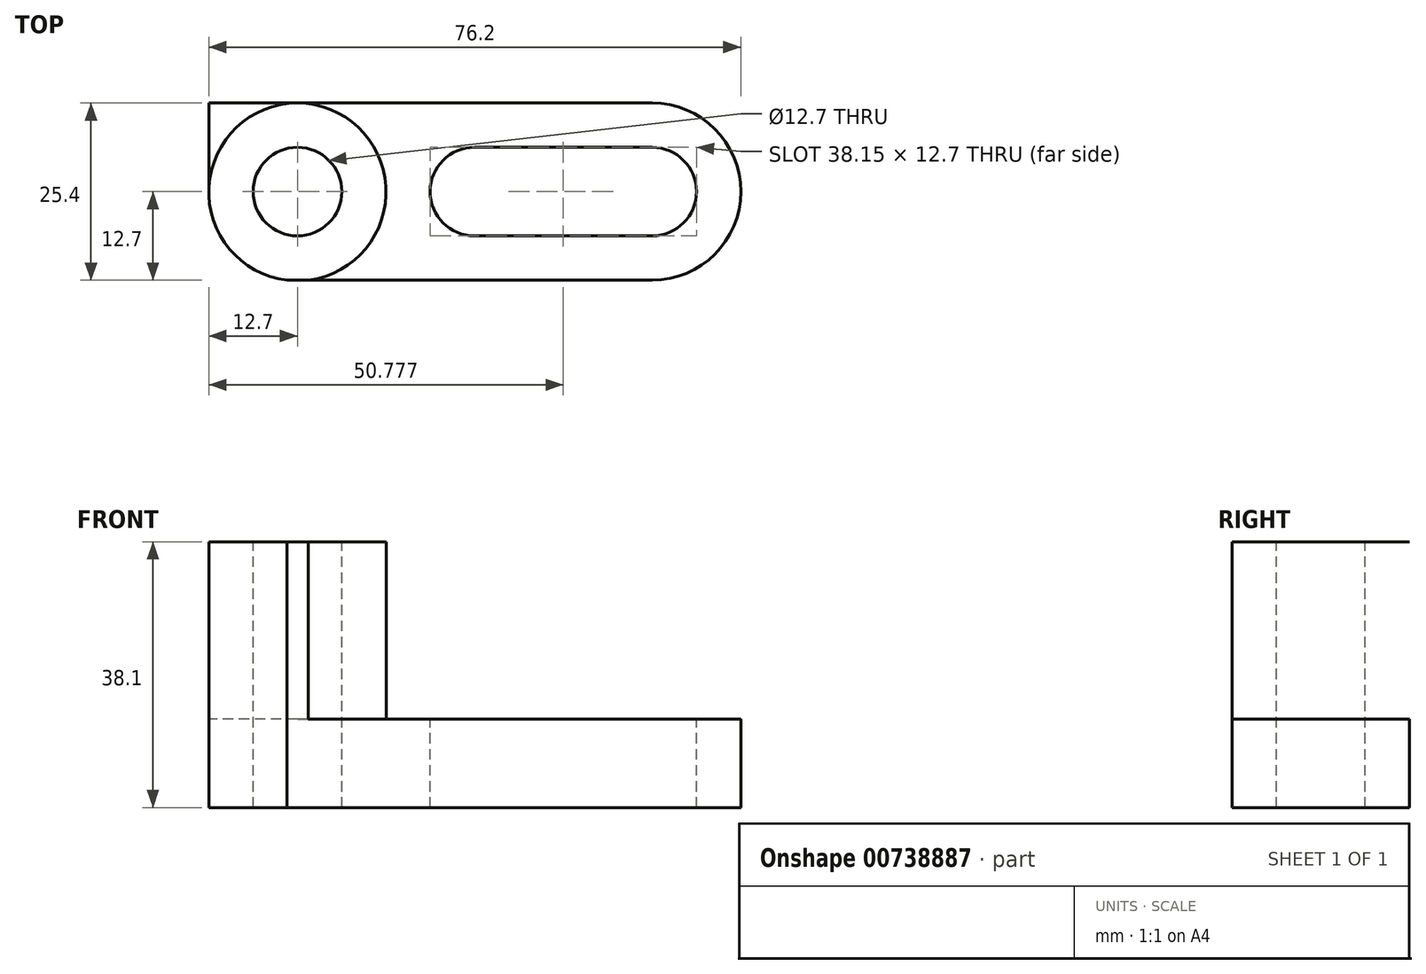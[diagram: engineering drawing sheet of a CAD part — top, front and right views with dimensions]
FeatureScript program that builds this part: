
annotation { "Feature Type Name" : "Feature", "Feature Type Description" : "" }
export const myFeature = defineFeature(function(context is Context, id is Id, definition is map)
    precondition{}
    {
        {
            var Q0;
            Q0=qCreatedBy(makeId("Front.planeOp"),FACE);
            var sketch = newSketch(context, id + "F0", { "sketchPlane" : qUnion([Q0])});
            skLineSegment(sketch, "E0", {"start": v(0, 38.1) * mm, "end": v(0, 0) * mm});
            skLineSegment(sketch, "E1", {"start": v(0, 0) * mm, "end": v(76.2, 0) * mm});
            skLineSegment(sketch, "E2", {"start": v(76.2, 0) * mm, "end": v(76.2, 38.1) * mm});
            skLineSegment(sketch, "E3", {"start": v(76.2, 38.1) * mm, "end": v(0, 38.1) * mm});
            skSolve(sketch);
        }
        {
            var Q0;
            Q0=makeQuery(id+"F0.imprint","IMPRINT",FACE,{"disambiguationData":[TD([[makeQuery(id+"F0.imprint","IMPRINT",EDGE,{"derivedFrom":sQuery(id+"F0.wireOp",EDGE,"E0")}),1.0]])]});
            extrude(context, id + "F1", {"entities" : qUnion([Q0]), "depth" : 25.4 * mm, "offsetDistance" : 25.4 * mm});
        }
        {
            var Q0;
            Q0=makeQuery(id+"F1.opExtrude","CAP_FACE",FACE,{"disambiguationData":[OSD([sQuery(id+"F0.wireOp",EDGE,"E0"),sQuery(id+"F0.wireOp",EDGE,"E1"),sQuery(id+"F0.wireOp",EDGE,"E2"),sQuery(id+"F0.wireOp",EDGE,"E3")])],"isStart":false});
            var sketch = newSketch(context, id + "F2", { "sketchPlane" : qUnion([Q0])});
            skLineSegment(sketch, "E4", {"start": v(25.4, 38.1) * mm, "end": v(25.4, 12.7) * mm});
            skLineSegment(sketch, "E5", {"start": v(25.4, 12.7) * mm, "end": v(76.2, 12.7) * mm});
            skSolve(sketch);
        }
        {
            var Q0;
            Q0 = qSketchRegion(id + "F2", true);
            var Q1;
            {var subQ0=sQuery(id+"F2.wireOp",EDGE,"E4");Q1=makeQuery(id+"F2.imprint","IMPRINT",FACE,{"disambiguationData":[TD([[makeQuery(id+"F2.imprint","IMPRINT",EDGE,{"derivedFrom":subQ0}),1.0]])]});}
            extrude(context, id + "F3", {"entities" : qUnion([Q0, Q1]), "operationType" : NewBodyOperationType.REMOVE, "oppositeDirection" : true, "depth" : 25.4 * mm, "offsetDistance" : 25.4 * mm});
        }
        {
            var Q0;
            Q0=makeQuery(id+"F1.opExtrude","SWEPT_FACE",FACE,{"disambiguationData":[OSD([sQuery(id+"F0.wireOp",EDGE,"E3")])]});
            var sketch = newSketch(context, id + "F4", { "sketchPlane" : qUnion([Q0])});
            skCircle(sketch, "E6", {"center": v(12.7, -12.7) * mm, "radius": 6.35 * mm});
            skArc(sketch, "E7", {"start": v(12.7, 0) * mm, "mid": v(0.02, -13.54) * mm, "end": v(14.28, -25.4) * mm});
            skArc(sketch, "E8", {"start": v(14.28, -25.4) * mm, "mid": v(25.38, -11.96) * mm, "end": v(12.7, 0) * mm});
            skSolve(sketch);
        }
        {
            var Q0;
            {var subQ0=sQuery(id+"F4.wireOp",EDGE,"E7");var subQ1=makeQuery(id+"F1.opExtrude","CAP_EDGE",EDGE,{"disambiguationData":[OSD([sQuery(id+"F0.wireOp",EDGE,"E3")])],"isStart":false});var subQ3=makeQuery(id+"F4.imprint","INTERSECT",VERTEX,{"derivedFrom":[subQ1,subQ0]});Q0=makeQuery(id+"F4.imprint","IMPRINT",FACE,{"disambiguationData":[TD([[makeQuery(id+"F4.imprint","IMPRINT",EDGE,{"disambiguationData":[TD([[subQ3,-1.0]])],"derivedFrom":subQ0}),1.0]])]});}
            var Q1;
            Q1=makeQuery(id+"F4.imprint","IMPRINT",FACE,{"disambiguationData":[TD([[makeQuery(id+"F4.imprint","IMPRINT",EDGE,{"derivedFrom":sQuery(id+"F4.wireOp",EDGE,"E6")}),1.0]])]});
            var Q2;
            {var subQ0=sQuery(id+"F4.wireOp",EDGE,"E7");var subQ1=sQuery(id+"F0.wireOp",EDGE,"E3");var subQ2=makeQuery(id+"F1.opExtrude","CAP_EDGE",EDGE,{"disambiguationData":[OSD([subQ1])],"isStart":true});var subQ3=makeQuery(id+"F4.imprint","INTERSECT",VERTEX,{"derivedFrom":[subQ2,subQ0,sQuery(id+"F4.wireOp",EDGE,"E8")]});Q2=makeQuery(id+"F4.imprint","IMPRINT",FACE,{"disambiguationData":[TD([[makeQuery(id+"F4.imprint","IMPRINT",EDGE,{"disambiguationData":[TD([[subQ3,-1.0]])],"derivedFrom":subQ0}),-1.0]])]});}
            var Q3;
            {var subQ0=sQuery(id+"F4.wireOp",EDGE,"E8");var subQ1=sQuery(id+"F0.wireOp",EDGE,"E3");var subQ2=makeQuery(id+"F1.opExtrude","CAP_EDGE",EDGE,{"disambiguationData":[OSD([subQ1])],"isStart":true});var subQ3=makeQuery(id+"F4.imprint","INTERSECT",VERTEX,{"derivedFrom":[subQ2,sQuery(id+"F4.wireOp",EDGE,"E7"),subQ0]});Q3=makeQuery(id+"F4.imprint","IMPRINT",FACE,{"disambiguationData":[TD([[makeQuery(id+"F4.imprint","IMPRINT",EDGE,{"disambiguationData":[TD([[subQ3,1.0]])],"derivedFrom":subQ0}),-1.0]])]});}
            var Q4;
            {var subQ0=sQuery(id+"F4.wireOp",EDGE,"E8");var subQ1=sQuery(id+"F0.wireOp",EDGE,"E3");var subQ2=makeQuery(id+"F1.opExtrude","CAP_EDGE",EDGE,{"disambiguationData":[OSD([subQ1])],"isStart":false});var subQ3=makeQuery(id+"F4.imprint","INTERSECT",VERTEX,{"derivedFrom":[subQ2,sQuery(id+"F4.wireOp",EDGE,"E7"),subQ0]});Q4=makeQuery(id+"F4.imprint","IMPRINT",FACE,{"disambiguationData":[TD([[makeQuery(id+"F4.imprint","IMPRINT",EDGE,{"disambiguationData":[TD([[subQ3,-1.0]])],"derivedFrom":subQ0}),-1.0]])]});}
            var Q5;
            {var subQ0=sQuery(id+"F4.wireOp",EDGE,"E7");var subQ1=sQuery(id+"F0.wireOp",EDGE,"E3");var subQ4=makeQuery(id+"F1.opExtrude","CAP_EDGE",EDGE,{"disambiguationData":[OSD([subQ1])],"isStart":false});var subQ5=makeQuery(id+"F4.imprint","INTERSECT",VERTEX,{"derivedFrom":[subQ4,subQ0]});Q5=makeQuery(id+"F4.imprint","IMPRINT",FACE,{"disambiguationData":[TD([[makeQuery(id+"F4.imprint","IMPRINT",EDGE,{"disambiguationData":[TD([[subQ5,1.0]])],"derivedFrom":subQ0}),-1.0]])]});}
            extrude(context, id + "F5", {"entities" : qUnion([Q0, Q1, Q2, Q3, Q4, Q5]), "operationType" : NewBodyOperationType.REMOVE, "oppositeDirection" : true, "depth" : 25.4 * mm, "offsetDistance" : 25.4 * mm});
        }
        {
            var Q0;
            {var subQ0=sQuery(id+"F0.wireOp",EDGE,"E3");var subQ1=makeQuery(id+"F1.opExtrude","CAP_EDGE",EDGE,{"disambiguationData":[OSD([subQ0])],"isStart":true});var subQ2=sQuery(id+"F0.wireOp",EDGE,"E0");var subQ3=makeQuery(id+"F1.opExtrude","SWEPT_EDGE",EDGE,{"disambiguationData":[OSD([subQ2,subQ0])]});var subQ4=makeQuery(id+"F4.imprint","INTERSECT",VERTEX,{"derivedFrom":[subQ3,subQ1]});var subQ5=sQuery(id+"F4.wireOp",EDGE,"E7");var subQ6=makeQuery(id+"F4.imprint","INTERSECT",VERTEX,{"derivedFrom":[subQ1,subQ5,sQuery(id+"F4.wireOp",EDGE,"E8")]});Q0=makeQuery(id+"F5.boolean.opBoolean","COPY",FACE,{"derivedFrom":makeQuery(id+"F5.opExtrude","CAP_FACE",FACE,{"disambiguationData":[OSD([subQ2,subQ0,subQ5]),TDD([makeQuery(id+"F4.imprint","IMPRINT",EDGE,{"disambiguationData":[TD([[subQ6,-1.0]])],"derivedFrom":subQ5}),makeQuery(id+"F4.imprint","IMPRINT",EDGE,{"disambiguationData":[TD([[subQ4,1.0]])],"derivedFrom":subQ3}),makeQuery(id+"F4.imprint","IMPRINT",EDGE,{"disambiguationData":[TD([[subQ4,1.0]])],"derivedFrom":subQ1})])],"isStart":false})});}
            var sketch = newSketch(context, id + "F6", { "sketchPlane" : qUnion([Q0])});
            skSolve(sketch);
        }
        {
            var Q0;
            Q0 = qSketchRegion(id + "F6", true);
            var Q1;
            {var subQ0=sQuery(id+"F4.wireOp",EDGE,"E7");var subQ1=sQuery(id+"F0.wireOp",EDGE,"E3");var subQ2=makeQuery(id+"F1.opExtrude","CAP_EDGE",EDGE,{"disambiguationData":[OSD([subQ1])],"isStart":true});var subQ3=makeQuery(id+"F4.imprint","INTERSECT",VERTEX,{"derivedFrom":[subQ2,subQ0,sQuery(id+"F4.wireOp",EDGE,"E8")]});Q1=makeQuery(id+"F6.imprint","IMPRINT",FACE,{"disambiguationData":[TD([[makeQuery(id+"F6.imprint","IMPRINT",EDGE,{"derivedFrom":makeQuery(id+"F5.boolean.opBoolean","COPY",EDGE,{"derivedFrom":makeQuery(id+"F5.opExtrude","CAP_EDGE",EDGE,{"disambiguationData":[OSD([subQ0]),TDD([makeQuery(id+"F4.imprint","IMPRINT",EDGE,{"disambiguationData":[TD([[subQ3,-1.0]])],"derivedFrom":subQ0})])],"isStart":false})})}),-1.0]])]});}
            var Q2;
            {var subQ0=sQuery(id+"F0.wireOp",EDGE,"E3");var subQ1=makeQuery(id+"F1.opExtrude","CAP_EDGE",EDGE,{"disambiguationData":[OSD([subQ0])],"isStart":false});var subQ2=sQuery(id+"F0.wireOp",EDGE,"E0");var subQ3=makeQuery(id+"F1.opExtrude","SWEPT_EDGE",EDGE,{"disambiguationData":[OSD([subQ2,subQ0])]});var subQ4=makeQuery(id+"F4.imprint","INTERSECT",VERTEX,{"derivedFrom":[subQ3,subQ1]});var subQ5=sQuery(id+"F4.wireOp",EDGE,"E7");var subQ6=makeQuery(id+"F4.imprint","INTERSECT",VERTEX,{"derivedFrom":[subQ1,subQ5]});Q2=makeQuery(id+"F5.boolean.opBoolean","COPY",FACE,{"derivedFrom":makeQuery(id+"F5.opExtrude","CAP_FACE",FACE,{"disambiguationData":[OSD([subQ2,subQ0,subQ5]),TDD([makeQuery(id+"F4.imprint","IMPRINT",EDGE,{"disambiguationData":[TD([[subQ6,1.0]])],"derivedFrom":subQ5}),makeQuery(id+"F4.imprint","IMPRINT",EDGE,{"disambiguationData":[TD([[subQ4,-1.0]])],"derivedFrom":subQ3}),makeQuery(id+"F4.imprint","IMPRINT",EDGE,{"disambiguationData":[TD([[subQ6,-1.0]])],"derivedFrom":subQ1})])],"isStart":false})});}
            extrude(context, id + "F7", {"entities" : qUnion([Q0, Q1, Q2]), "operationType" : NewBodyOperationType.REMOVE, "oppositeDirection" : true, "depth" : 25.4 * mm, "offsetDistance" : 25.4 * mm});
        }
        {
            var Q0;
            Q0=makeQuery(id+"F5.boolean.opBoolean","COPY",FACE,{"derivedFrom":makeQuery(id+"F5.opExtrude","CAP_FACE",FACE,{"disambiguationData":[OSD([sQuery(id+"F4.wireOp",EDGE,"E6")])],"isStart":false})});
            extrude(context, id + "F8", {"entities" : qUnion([Q0]), "operationType" : NewBodyOperationType.REMOVE, "oppositeDirection" : true, "depth" : 25.4 * mm, "offsetDistance" : 25.4 * mm});
        }
        {
            var Q0;
            {var subQ0=sQuery(id+"F0.wireOp",EDGE,"E3");var subQ1=makeQuery(id+"F1.opExtrude","CAP_EDGE",EDGE,{"disambiguationData":[OSD([subQ0])],"isStart":true});var subQ2=sQuery(id+"F2.wireOp",EDGE,"E4");var subQ3=makeQuery(id+"F3.boolean.opBoolean","COPY",EDGE,{"derivedFrom":makeQuery(id+"F3.opExtrude","SWEPT_EDGE",EDGE,{"disambiguationData":[OSD([subQ0,subQ2])]})});var subQ4=makeQuery(id+"F4.imprint","INTERSECT",VERTEX,{"derivedFrom":[subQ3,subQ1]});var subQ5=sQuery(id+"F4.wireOp",EDGE,"E8");var subQ6=sQuery(id+"F4.wireOp",EDGE,"E7");var subQ7=makeQuery(id+"F4.imprint","INTERSECT",VERTEX,{"derivedFrom":[subQ1,subQ6,subQ5]});var subQ9=makeQuery(id+"F1.opExtrude","CAP_EDGE",EDGE,{"disambiguationData":[OSD([subQ0])],"isStart":false});var subQ10=makeQuery(id+"F4.imprint","INTERSECT",VERTEX,{"derivedFrom":[subQ3,subQ9]});var subQ11=makeQuery(id+"F4.imprint","INTERSECT",VERTEX,{"derivedFrom":[subQ9,subQ6,subQ5]});Q0=makeQuery(id+"F5.boolean.opBoolean","MERGE",FACE,{"derivedFrom":[makeQuery(id+"F3.boolean.opBoolean","COPY",FACE,{"derivedFrom":makeQuery(id+"F3.opExtrude","SWEPT_FACE",FACE,{"disambiguationData":[OSD([sQuery(id+"F2.wireOp",EDGE,"E5")])]})}),makeQuery(id+"F5.opExtrude","CAP_FACE",FACE,{"disambiguationData":[OSD([subQ0,subQ2,subQ5]),TDD([makeQuery(id+"F4.imprint","IMPRINT",EDGE,{"disambiguationData":[TD([[subQ11,-1.0]])],"derivedFrom":subQ5}),makeQuery(id+"F4.imprint","IMPRINT",EDGE,{"disambiguationData":[TD([[subQ10,1.0]])],"derivedFrom":subQ3}),makeQuery(id+"F4.imprint","IMPRINT",EDGE,{"disambiguationData":[TD([[subQ10,-1.0]])],"derivedFrom":subQ9})])],"isStart":false}),makeQuery(id+"F5.opExtrude","CAP_FACE",FACE,{"disambiguationData":[OSD([subQ0,subQ2,subQ5]),TDD([makeQuery(id+"F4.imprint","IMPRINT",EDGE,{"disambiguationData":[TD([[subQ7,1.0]])],"derivedFrom":subQ5}),makeQuery(id+"F4.imprint","IMPRINT",EDGE,{"disambiguationData":[TD([[subQ4,-1.0]])],"derivedFrom":subQ3}),makeQuery(id+"F4.imprint","IMPRINT",EDGE,{"disambiguationData":[TD([[subQ4,-1.0]])],"derivedFrom":subQ1})])],"isStart":false})]});}
            var sketch = newSketch(context, id + "F9", { "sketchPlane" : qUnion([Q0])});
            skCircle(sketch, "E9", {"center": v(38.05, -12.7) * mm, "radius": 6.35 * mm});
            skCircle(sketch, "E10", {"center": v(63.5, -12.7) * mm, "radius": 6.35 * mm});
            skLineSegment(sketch, "E11", {"start": v(38.05, -19.05) * mm, "end": v(63.5, -19.05) * mm});
            skLineSegment(sketch, "E12", {"start": v(38.05, -6.35) * mm, "end": v(63.5, -6.35) * mm});
            skArc(sketch, "E13", {"start": v(63.5, -25.4) * mm, "mid": v(76.2, -12.7) * mm, "end": v(63.5, 0) * mm});
            skSolve(sketch);
        }
        {
            var Q0;
            Q0 = qSketchRegion(id + "F9", true);
            var Q1;
            {var subQ0=sQuery(id+"F9.wireOp",EDGE,"E13");var subQ3=sQuery(id+"F2.wireOp",EDGE,"E5");var subQ6=makeQuery(id+"F3.boolean.opBoolean","COPY",EDGE,{"derivedFrom":makeQuery(id+"F3.opExtrude","SWEPT_EDGE",EDGE,{"disambiguationData":[OSD([sQuery(id+"F0.wireOp",EDGE,"E2"),subQ3])]})});var subQ7=makeQuery(id+"F9.imprint","INTERSECT",VERTEX,{"derivedFrom":[subQ6,subQ0]});Q1=makeQuery(id+"F9.imprint","IMPRINT",FACE,{"disambiguationData":[TD([[makeQuery(id+"F9.imprint","IMPRINT",EDGE,{"disambiguationData":[TD([[subQ7,-1.0]])],"derivedFrom":subQ0}),-1.0]])]});}
            var Q2;
            {var subQ0=sQuery(id+"F9.wireOp",EDGE,"E13");var subQ3=sQuery(id+"F2.wireOp",EDGE,"E5");var subQ6=makeQuery(id+"F3.boolean.opBoolean","COPY",EDGE,{"derivedFrom":makeQuery(id+"F3.opExtrude","SWEPT_EDGE",EDGE,{"disambiguationData":[OSD([sQuery(id+"F0.wireOp",EDGE,"E2"),subQ3])]})});var subQ7=makeQuery(id+"F9.imprint","INTERSECT",VERTEX,{"derivedFrom":[subQ6,subQ0]});Q2=makeQuery(id+"F9.imprint","IMPRINT",FACE,{"disambiguationData":[TD([[makeQuery(id+"F9.imprint","IMPRINT",EDGE,{"disambiguationData":[TD([[subQ7,1.0]])],"derivedFrom":subQ0}),-1.0]])]});}
            extrude(context, id + "F10", {"entities" : qUnion([Q0, Q1, Q2]), "operationType" : NewBodyOperationType.REMOVE, "oppositeDirection" : true, "depth" : 25.4 * mm, "offsetDistance" : 25.4 * mm});
        }
    });
